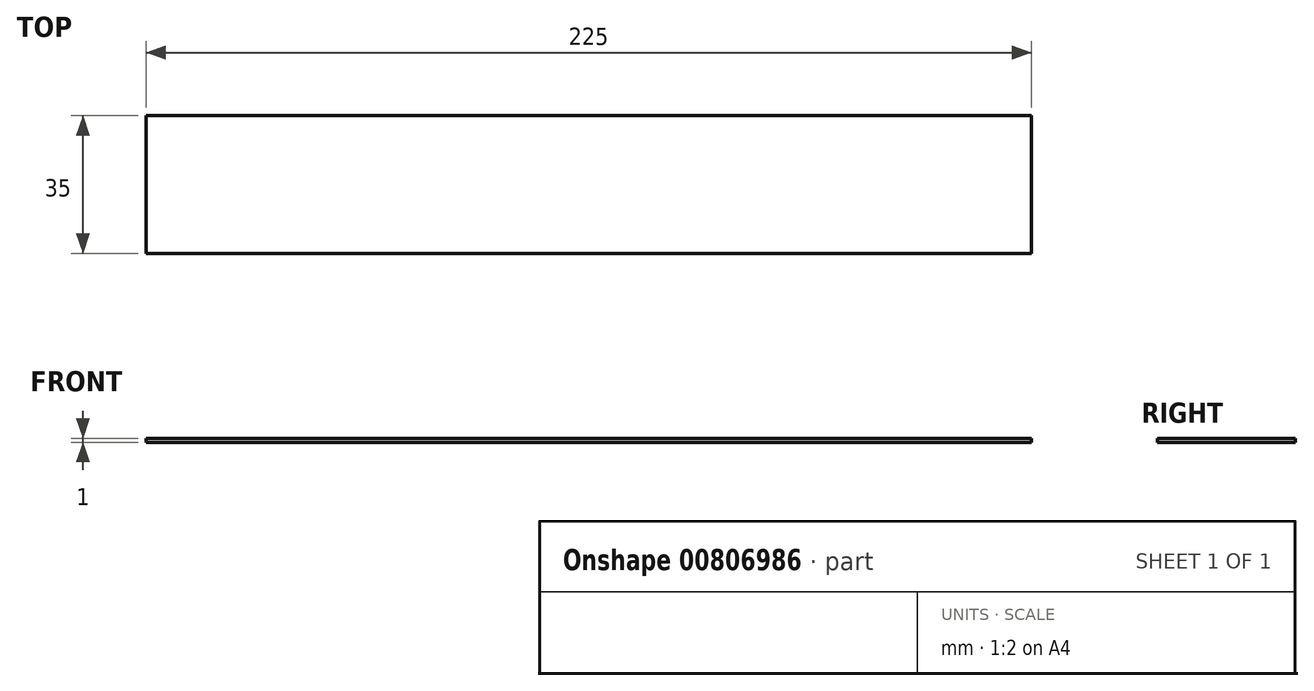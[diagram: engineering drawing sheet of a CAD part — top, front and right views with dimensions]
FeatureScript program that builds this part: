
annotation { "Feature Type Name" : "Feature", "Feature Type Description" : "" }
export const myFeature = defineFeature(function(context is Context, id is Id, definition is map)
    precondition{}
    {
        {
            var Q0;
            Q0=qCreatedBy(makeId("Top.planeOp"),FACE);
            var sketch = newSketch(context, id + "F0", { "sketchPlane" : qUnion([Q0])});
            skLineSegment(sketch, "E0.bottom", {"start": v(-113, 17.5) * mm, "end": v(112, 17.5) * mm});
            skLineSegment(sketch, "E0.top", {"start": v(-113, -17.5) * mm, "end": v(112, -17.5) * mm});
            skLineSegment(sketch, "E0.left", {"start": v(-113, 17.5) * mm, "end": v(-113, -17.5) * mm});
            skLineSegment(sketch, "E0.right", {"start": v(112, 17.5) * mm, "end": v(112, -17.5) * mm});
            skSolve(sketch);
        }
        {
            var Q0;
            Q0=makeQuery(id+"F0.imprint","IMPRINT",FACE,{"disambiguationData":[TD([[makeQuery(id+"F0.imprint","IMPRINT",EDGE,{"derivedFrom":sQuery(id+"F0.wireOp",EDGE,"E0.bottom")}),-1.0]])]});
            extrude(context, id + "F1", {"entities" : qUnion([Q0]), "depth" : 1 * mm, "offsetDistance" : 25 * mm});
        }
    });
